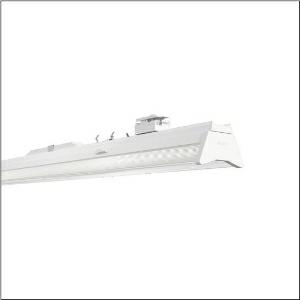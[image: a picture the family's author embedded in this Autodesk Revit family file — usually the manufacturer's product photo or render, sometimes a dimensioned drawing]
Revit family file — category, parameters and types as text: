
# Revit family: licross_r__11_performance_mo_51td16dn445g_6250
name_source: partatom
category: Lighting Fixtures
units: mm (PartAtom-declared; Revit-internal decimal feet)

## family parameters
Cut with Voids When Loaded = No
Host = Face
Light Source = No
Part Type = Normal
Room Calculation Point = No
Round Connector Dimension = Use Diameter
Shared = No

## types (1)
- --- (1 x LED, 4520 lm, 24.3 W, 4000K)
    Apparent Load = 24 VA
    CIE Flux Codes = 66 88 96 79 100
    Color Rendering = 80
    Color Temperature = 4000K
    Default Elevation = 1800 mm
    Description = Licross® 11 Performance MO, luminaire insert, of sheet steel, galvanised, coil coated, white, length: 1.500mm, width: 120mm, height: 123mm, LED rated luminous flux: 4.520lm, light colour: 840, control gear: DALI 2, with plug, 5-pole, with phase selection, mains connection: 220..240V, AC, 50/60Hz, rated input power: 24W, internal wiring halogen-free, primary light control with lens, of plastic, primary optical cover: cover, of PMMA, CAT 2 (L<= 3000cd/m²), light emission: direct/indirect distribution, primary light characteristic: symmetric, protection rating (complete): IP54, insulation class (complete): insulation class I (protective earthing), certification: CE, ENEC, VDE, UKCA, protection symbol: D if used in an environment with non-conductive dust loads with corresponding accessories, impact resistance: IK06, permissible ambient temperature for indoor applications: -25..+45°C, corresponds to IFS (International Featured Standards) requirements for safety and quality in the food industry, reducing of maximum allowable ambient temperature of 5°C with ceiling mounting, LABS conformity tested according to VDMA 24364:2018-05, packaging unit: 1 piece
    Height = 114 mm
    Lamp = 1 x LED
    Lamp Light Flux = 4520 lm
    Lamp Power = 24.3 W
    Lamp count = 1
    Length = 1500 mm
    Luminous efficacy = 186 lm/W
    Manufacturer = Siteco
    ModVariant = No
    Model = 51TD16DN445G
    Mounting Place = Ceiling
    Mounting Type = Pendant
    Number of Poles = 1
    OnlyDefault = Yes
    Power Factor = 1
    Product Name = Licross® 11 Performance MO
    Product group = luminaire insert | ceiling pendant
    ProductGroupID = 902
    Protection Class = Protection class I
    Protection Degree = IP 54
    RLX_Detail_Level = 1
    RLX_Emergency_Light_Flux = 0 lm
    RLX_Emergency_Type = 0
    RLX_Emergency_Type_DB = No
    RlxData = <blob elided: 33793 chars, md5=40ba1776>
    Socket = socket
    Standby Power = 0 W
    System Light Flux = 4520 lm
    System Power = 24 W
    Type Comments = factory setting: luminous flux: 100 % | dim-lin: 254 | 161 mA
    Type Image = l_1256138.jpg
    URL = http://relux.com
    VarID = @adj_084593
    Voltage = 0 V
    Weight = 0.00 kg
    Width = 120 mm

## geometry (parser evidence)
native form markers: Blend x4, Sweep x12
no freeform markers — native parametric forms only
